# Revit family: Sanitary_Sanitary-Taps-Mixers_hansgrohe_31846XXX-Focus-M41-Single-lever-kitchen_
name_source: partatom
category: Plumbing Fixtures
revit_build: Autodesk Revit 2018 (Build: 20170223_1515(x64)
units: mm (PartAtom-declared; Revit-internal decimal feet)

## family parameters
Always vertical = No
Cut with Voids When Loaded = No
OmniClass Number = 23.45.00.00
OmniClass Title = Sanitary, Laundry, and Cleaning Equipment
Part Type = Normal
Room Calculation Point = No
Round Connector Dimension = Use Diameter
Shared = No
Work Plane-Based = Yes

## types (2) — shared parameters
Always visible = Yes
BIMobject category = Sanitary Taps & Mixers
Default Elevation = 1219.2 mm  [stored 4 ft]
Design country = Germany
EAN code = 4059625295229
Edition number = 1
GTIN code = https://4059625295229
IFC Classification = Sanitary Terminal
Installation instructions = https://www.hansgrohe.com
Manufacturer country = Germany
Manufacturer name = hansgrohe
Masterformat 2014 Code = 41 14 33
Masterformat 2014 Description = Mixers
Material secondary = Chrome
NBS Reference Code = 35-06-82
NBS Reference Description = Shower Mixers
Product Guid = 2bb1693d-0469-444f-9bc0-cabf77b4cd86
Product SKU = 31846XXX
Product data url = https://www.bimobject.com
Product family = Focus M41
Product group = Kitchen mixers
Product name = 31846XXX Focus M41 Single lever kitchen mixer 240, pull-out spray, 2jet, DZR
Product url = https://www.hansgrohe.com
QR code = https://www.bimobject.com
Technical description = https://www.hansgrohe.com
Uniclass 2.0 Code = PR-35-06-82
Uniclass 2.0 Description = Shower Mixers
Uniclass 2015 Code = Pr_60_75_08_54
Uniclass 2015 Name = Mixers
Weight Net (Kg) = 2,8

## per-type parameters (varying)
| type | Material 1 |
| 670 Matte Black | Hansgrohe - Metal - 670 Matte Black |
| 000 Chrome | Hansgrohe - Metal - 000 Chrome |

note: [stored X ft] marks values corroborated as IEEE doubles in the binary element streams (Revit-internal decimal feet)

## geometry (parser evidence)
native form markers: Sweep x2
no freeform markers — native parametric forms only
